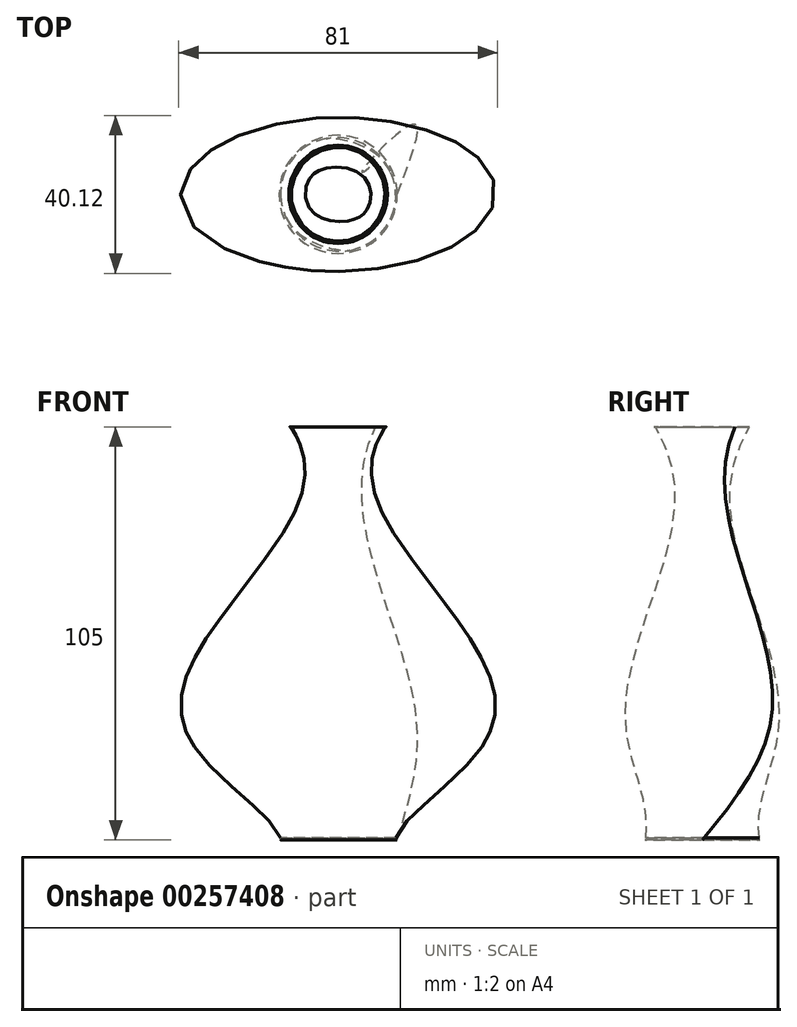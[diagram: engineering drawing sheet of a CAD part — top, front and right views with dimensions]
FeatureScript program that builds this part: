
annotation { "Feature Type Name" : "Feature", "Feature Type Description" : "" }
export const myFeature = defineFeature(function(context is Context, id is Id, definition is map)
    precondition{}
    {
        {
            var Q0;
            Q0=qCreatedBy(makeId("Top.planeOp"),FACE);
            var sketch = newSketch(context, id + "F0", { "sketchPlane" : qUnion([Q0])});
            skCircle(sketch, "E0", {"center": v(0, 0) * mm, "radius": 15 * mm});
            skSolve(sketch);
        }
        {
            var Q0;
            Q0=qCreatedBy(makeId("Top.planeOp"),FACE);
            cPlane(context, id + "F1", {"entities" : qUnion([Q0]), "cplaneType" : CPlaneType.OFFSET, "offset" : 30 * mm, "width" : 150 * mm, "height" : 150 * mm});
        }
        {
            var Q0;
            Q0=qCreatedBy(id+"F1.planeOp",FACE);
            var sketch = newSketch(context, id + "F2", { "sketchPlane" : qUnion([Q0])});
            skEllipse(sketch, "E1", {"center": v(0, 0) * mm, "majorRadius": 20 * mm, "minorRadius": 40 * mm, "majorAxis": v(0, 1)});
            skSolve(sketch);
        }
        {
            var Q0;
            Q0=qCreatedBy(makeId("Top.planeOp"),FACE);
            cPlane(context, id + "F3", {"entities" : qUnion([Q0]), "cplaneType" : CPlaneType.OFFSET, "offset" : 100 * mm, "width" : 150 * mm, "height" : 150 * mm});
        }
        {
            var Q0;
            Q0=qCreatedBy(makeId("Top.planeOp"),FACE);
            cPlane(context, id + "F4", {"entities" : qUnion([Q0]), "cplaneType" : CPlaneType.OFFSET, "offset" : 105 * mm, "width" : 150 * mm, "height" : 150 * mm});
        }
        {
            var Q0;
            Q0=qCreatedBy(id+"F3.planeOp",FACE);
            var sketch = newSketch(context, id + "F5", { "sketchPlane" : qUnion([Q0])});
            skCircle(sketch, "E2", {"center": v(0, 0) * mm, "radius": 10 * mm});
            skSolve(sketch);
        }
        {
            var Q0;
            Q0=qCreatedBy(id+"F4.planeOp",FACE);
            var sketch = newSketch(context, id + "F6", { "sketchPlane" : qUnion([Q0])});
            skCircle(sketch, "E3", {"center": v(0, 0) * mm, "radius": 12.5 * mm});
            skSolve(sketch);
        }
        {
            var Q0;
            Q0=makeQuery(id+"F0.imprint","IMPRINT",FACE,{"disambiguationData":[TD([[makeQuery(id+"F0.imprint","IMPRINT",EDGE,{"derivedFrom":sQuery(id+"F0.wireOp",EDGE,"E0")}),1.0]])]});
            var Q1;
            Q1=makeQuery(id+"F2.imprint","IMPRINT",FACE,{"disambiguationData":[TD([[makeQuery(id+"F2.imprint","IMPRINT",EDGE,{"derivedFrom":sQuery(id+"F2.wireOp",EDGE,"E1")}),1.0]])]});
            var Q2;
            Q2=makeQuery(id+"F5.imprint","IMPRINT",FACE,{"disambiguationData":[TD([[makeQuery(id+"F5.imprint","IMPRINT",EDGE,{"derivedFrom":sQuery(id+"F5.wireOp",EDGE,"E2")}),1.0]])]});
            var Q3;
            Q3=makeQuery(id+"F6.imprint","IMPRINT",FACE,{"disambiguationData":[TD([[makeQuery(id+"F6.imprint","IMPRINT",EDGE,{"derivedFrom":sQuery(id+"F6.wireOp",EDGE,"E3")}),1.0]])]});
            loft(context, id + "F7", {"sheetProfilesArray" : [{ "sheetProfileEntities" : qUnion([Q0]) }, { "sheetProfileEntities" : qUnion([Q1]) }, { "sheetProfileEntities" : qUnion([Q2]) }, { "sheetProfileEntities" : qUnion([Q3]) }]});
        }
        {
            var Q0;
            Q0=makeQuery(id+"F7.opLoft","CAP_FACE",FACE,{"disambiguationData":[OSD([makeQuery(id+"F6.imprint","IMPRINT",FACE,{"disambiguationData":[TD([[makeQuery(id+"F6.imprint","IMPRINT",EDGE,{"derivedFrom":sQuery(id+"F6.wireOp",EDGE,"E3")}),1.0]])]})])],"isStart":true});
            shell(context, id + "F8", {"entities" : qUnion([Q0]), "thickness" : 0.5 * mm});
        }
    });
